# Revit family: AL-870
name_source: partatom
category: Plumbing Fixtures
revit_build: Autodesk Revit Architecture 2012 (Build: 20110309_2315(x64)
units: mm (PartAtom-declared; Revit-internal decimal feet)

## types (1)
- AL-870
    Aerated flow handspray = C-071-CP
    Angle regulating valves with sliding wall flanges = 232-10
    Assembly Code = D2010
    CW Connection = Yes
    CWFU = 0
    Cartridge = S-750-1SINK
    Connection tubes = C-M10X1/2
    Cost = 0 $
    Default Elevation = 0' - 0"
    Description = Single lever with swivel hand set support tube + angle valves. 1/2"BSP FI
    Flexible handshower hose = 008SP
    HW Connection = Yes
    HWFU = 0
    Keynote = 1/2" female iron 400mm long flexible inlets
    Manufacturer = COBRA
    Material = Chrome - Polished
    Model = AL-870
    Range = Aplos
    Straight hose adaptor = C-071-2-CP
    Type Comments = SANS 1480
    URL = http://www.cobra.co.za
    Vent Connection = No
    WFU = 0
    Waste Connection = No

## geometry (parser evidence)
native form markers: Blend x2
no freeform markers — native parametric forms only
